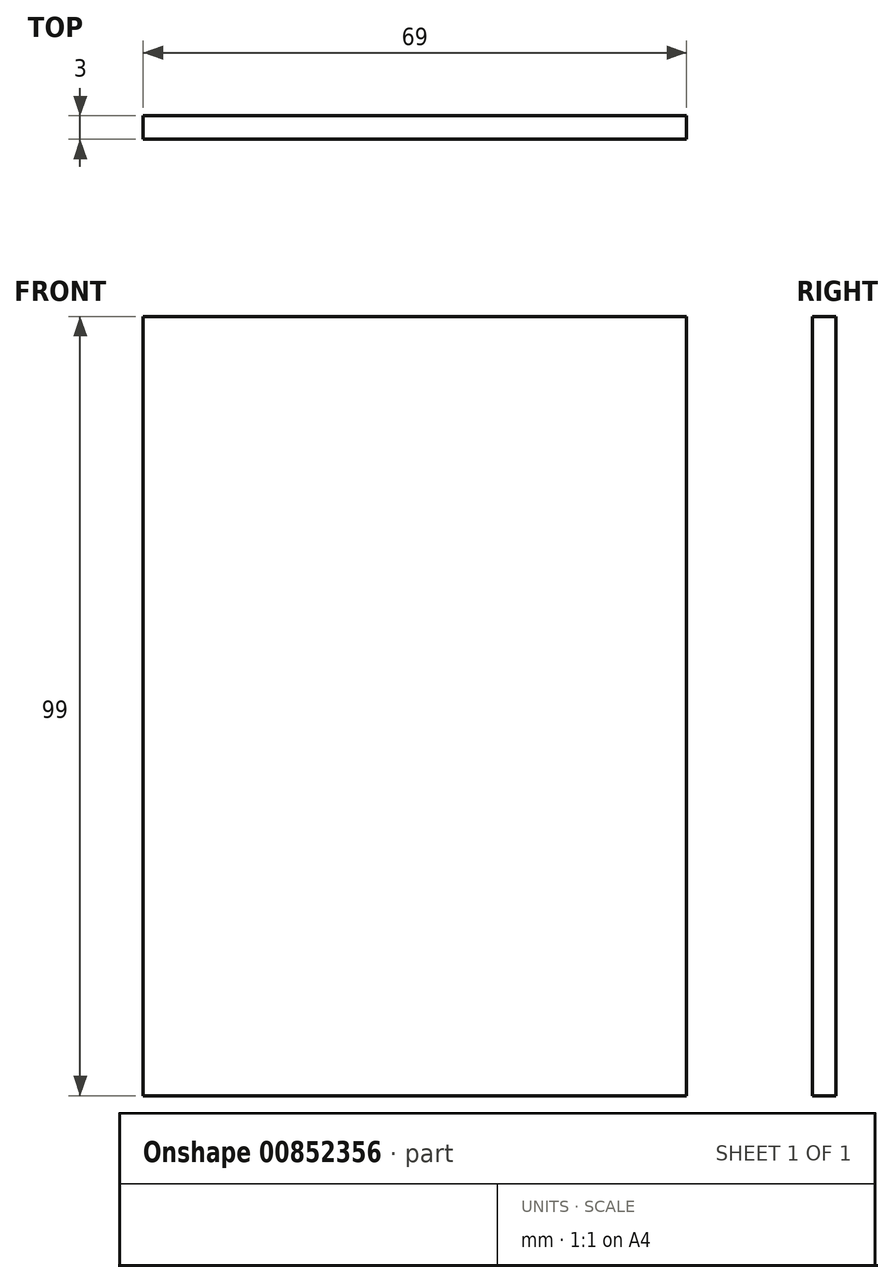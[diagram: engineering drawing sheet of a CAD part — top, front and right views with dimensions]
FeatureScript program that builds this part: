
annotation { "Feature Type Name" : "Feature", "Feature Type Description" : "" }
export const myFeature = defineFeature(function(context is Context, id is Id, definition is map)
    precondition{}
    {
        {
            var Q0;
            Q0=qCreatedBy(makeId("Front.planeOp"),FACE);
            var sketch = newSketch(context, id + "F0", { "sketchPlane" : qUnion([Q0])});
            skLineSegment(sketch, "E0.bottom", {"start": v(-38.49, 43.69) * mm, "end": v(30.51, 43.69) * mm});
            skLineSegment(sketch, "E0.top", {"start": v(-38.49, -55.31) * mm, "end": v(30.51, -55.31) * mm});
            skLineSegment(sketch, "E0.left", {"start": v(-38.49, 43.69) * mm, "end": v(-38.49, -55.31) * mm});
            skLineSegment(sketch, "E0.right", {"start": v(30.51, 43.69) * mm, "end": v(30.51, -55.31) * mm});
            skSolve(sketch);
        }
        {
            var Q0;
            Q0=makeQuery(id+"F0.imprint","IMPRINT",FACE,{"disambiguationData":[TD([[makeQuery(id+"F0.imprint","IMPRINT",EDGE,{"derivedFrom":sQuery(id+"F0.wireOp",EDGE,"E0.bottom")}),-1.0]])]});
            extrude(context, id + "F1", {"entities" : qUnion([Q0]), "depth" : 3 * mm, "offsetDistance" : 25.4 * mm});
        }
    });
